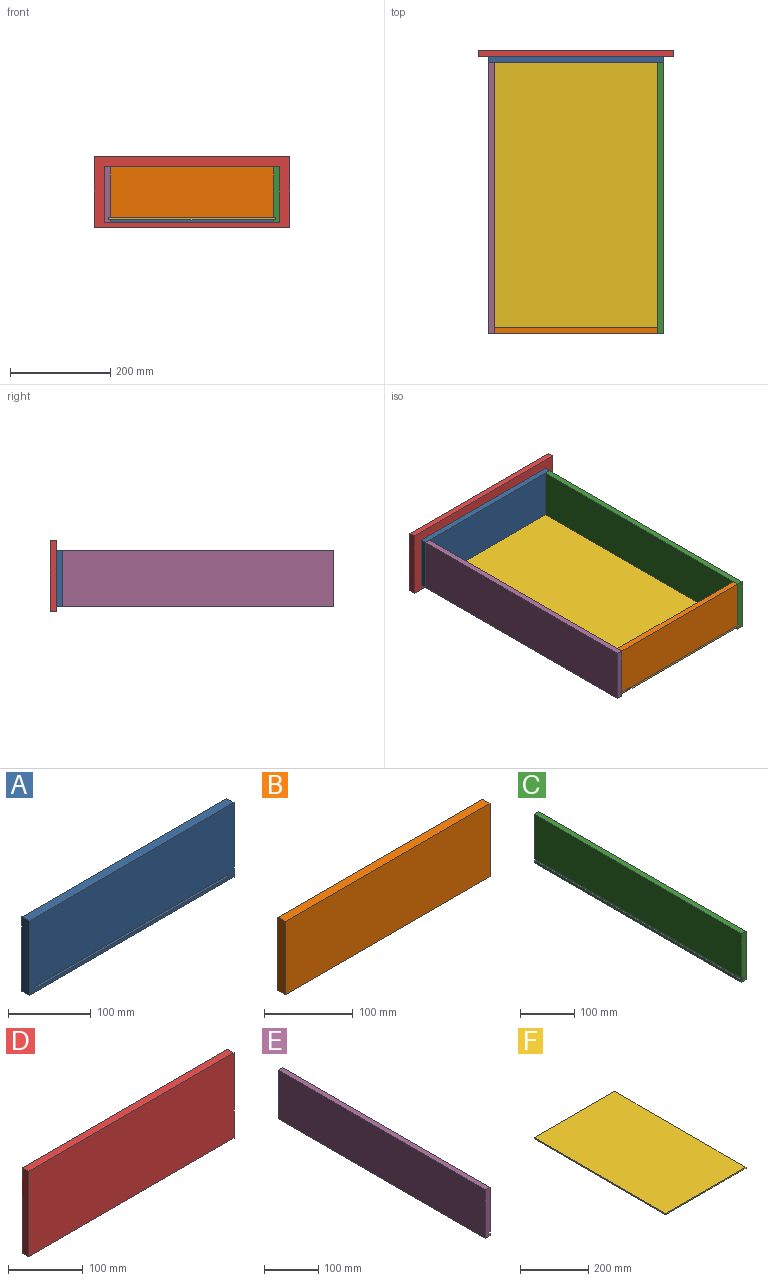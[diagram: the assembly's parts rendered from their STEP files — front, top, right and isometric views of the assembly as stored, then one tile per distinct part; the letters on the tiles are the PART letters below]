
ASSEMBLY  parts=6 mates=5
PART A: 11 faces, bbox 350x12x110 mm
  f0: plane 110x12mm, normal (-1,0,0), area 1320mm2, adj f1,f3,f4,f5
  f1: plane 350x12mm, normal (0,0,-1), area 4200mm2, adj f0,f2,f4,f5
  f2: plane 110x12mm, normal (1,0,0), area 1320mm2, adj f1,f3,f4,f5
  f3: plane 350x12mm, normal (0,0,1), area 4200mm2, adj f0,f2,f4,f5
  f4: plane 350x110mm, normal (0,-1,0), area 37172mm2, adj f0,f1,f2,f3,f6,f7,f8,f9
  f5: plane 350x110mm, normal (0,1,0), area 38500mm2, adj f0,f1,f2,f3
  f6: plane 332x3mm, normal (0,0,1), area 996mm2, adj f4,f7,f9,f10
  f7: plane 4x3mm, normal (-1,0,0), area 12mm2, adj f4,f6,f8,f10
  f8: plane 332x3mm, normal (0,0,-1), area 996mm2, adj f4,f7,f9,f10
  f9: plane 4x3mm, normal (1,0,0), area 12mm2, adj f4,f6,f8,f10
  f10: plane 332x4mm, normal (0,-1,0), area 1328mm2, adj f6,f7,f8,f9
PART B: 6 faces, bbox 326x12x101 mm
  f0: plane 326x12mm, normal (0,0,1), area 3912mm2, adj f1,f3,f4,f5
  f1: plane 101x12mm, normal (-1,0,0), area 1212mm2, adj f0,f2,f4,f5
  f2: plane 326x12mm, normal (0,0,-1), area 3912mm2, adj f1,f3,f4,f5
  f3: plane 101x12mm, normal (1,0,0), area 1212mm2, adj f0,f2,f4,f5
  f4: plane 326x101mm, normal (0,1,0), area 32926mm2, adj f0,f1,f2,f3
  f5: plane 326x101mm, normal (0,-1,0), area 32926mm2, adj f0,f1,f2,f3
PART C: 10 faces, bbox 12x541x110 mm
  f0: plane 541x3mm, normal (0,0,1), area 1623mm2, adj f1,f7,f8,f9
  f1: plane 541x5mm, normal (-1,0,0), area 2705mm2, adj f0,f2,f8,f9
  f2: plane 541x12mm, normal (0,0,-1), area 6492mm2, adj f1,f3,f8,f9
  f3: plane 541x110mm, normal (1,0,0), area 59510mm2, adj f2,f4,f8,f9
  f4: plane 541x12mm, normal (0,0,1), area 6492mm2, adj f3,f5,f8,f9
  f5: plane 541x101mm, normal (-1,0,0), area 54641mm2, adj f4,f6,f8,f9
  f6: plane 541x3mm, normal (0,0,-1), area 1623mm2, adj f5,f7,f8,f9
  f7: plane 541x4mm, normal (-1,0,0), area 2164mm2, adj f0,f6,f8,f9
  f8: plane 110x12mm, normal (0,-1,0), area 1308mm2, adj f0,f1,f2,f3,f4,f5,f6,f7
  f9: plane 110x12mm, normal (0,1,0), area 1308mm2, adj f0,f1,f2,f3,f4,f5,f6,f7
PART D: 6 faces, bbox 390x12x140 mm
  f0: plane 390x12mm, normal (0,0,1), area 4680mm2, adj f1,f3,f4,f5
  f1: plane 140x12mm, normal (-1,0,0), area 1680mm2, adj f0,f2,f4,f5
  f2: plane 390x12mm, normal (0,0,-1), area 4680mm2, adj f1,f3,f4,f5
  f3: plane 140x12mm, normal (1,0,0), area 1680mm2, adj f0,f2,f4,f5
  f4: plane 390x140mm, normal (0,1,0), area 54600mm2, adj f0,f1,f2,f3
  f5: plane 390x140mm, normal (0,-1,0), area 54600mm2, adj f0,f1,f2,f3
PART E: 10 faces, bbox 12x541x110 mm
  f0: plane 541x12mm, normal (0,0,-1), area 6492mm2, adj f1,f7,f8,f9
  f1: plane 541x5mm, normal (1,0,0), area 2705mm2, adj f0,f2,f8,f9
  f2: plane 541x3mm, normal (0,0,1), area 1623mm2, adj f1,f3,f8,f9
  f3: plane 541x4mm, normal (1,0,0), area 2164mm2, adj f2,f4,f8,f9
  f4: plane 541x3mm, normal (0,0,-1), area 1623mm2, adj f3,f5,f8,f9
  f5: plane 541x101mm, normal (1,0,0), area 54641mm2, adj f4,f6,f8,f9
  f6: plane 541x12mm, normal (0,0,1), area 6492mm2, adj f5,f7,f8,f9
  f7: plane 541x110mm, normal (-1,0,0), area 59510mm2, adj f0,f6,f8,f9
  f8: plane 110x12mm, normal (0,-1,0), area 1308mm2, adj f0,f1,f2,f3,f4,f5,f6,f7
  f9: plane 110x12mm, normal (0,1,0), area 1308mm2, adj f0,f1,f2,f3,f4,f5,f6,f7
PART F: 6 faces, bbox 332x544x4 mm
  f0: plane 332x4mm, normal (0,-1,0), area 1328mm2, adj f1,f3,f4,f5
  f1: plane 544x4mm, normal (-1,0,0), area 2176mm2, adj f0,f2,f4,f5
  f2: plane 332x4mm, normal (0,1,0), area 1328mm2, adj f1,f3,f4,f5
  f3: plane 544x4mm, normal (1,0,0), area 2176mm2, adj f0,f2,f4,f5
  f4: plane 544x332mm, normal (0,0,-1), area 180608mm2, adj f0,f1,f2,f3
  f5: plane 544x332mm, normal (0,0,1), area 180608mm2, adj f0,f1,f2,f3
PLACE A t=(0,0,5)mm fixed
PLACE B t=(0,0,5)mm
PLACE C t=(0,0,5)mm
PLACE D t=(0,0,5)mm
PLACE E t=(0,0,5)mm
PLACE F t=(0,0,5)mm
MATE fastened A.f10 <-> F.f2  axis (0,-1,0) through (0,-9,-48)mm
MATE fastened B.f3 <-> C.f5  axis (1,0,0) through (163,-553,55)mm
MATE fastened E.f9 <-> A.f4  axis (0,1,0) through (-175,-12,55)mm
MATE fastened A.f4 <-> C.f9  axis (0,-1,0) through (175,-12,55)mm
MATE fastened A.f5 <-> D.f5  axis (0,1,0) through (0,0,0)mm
